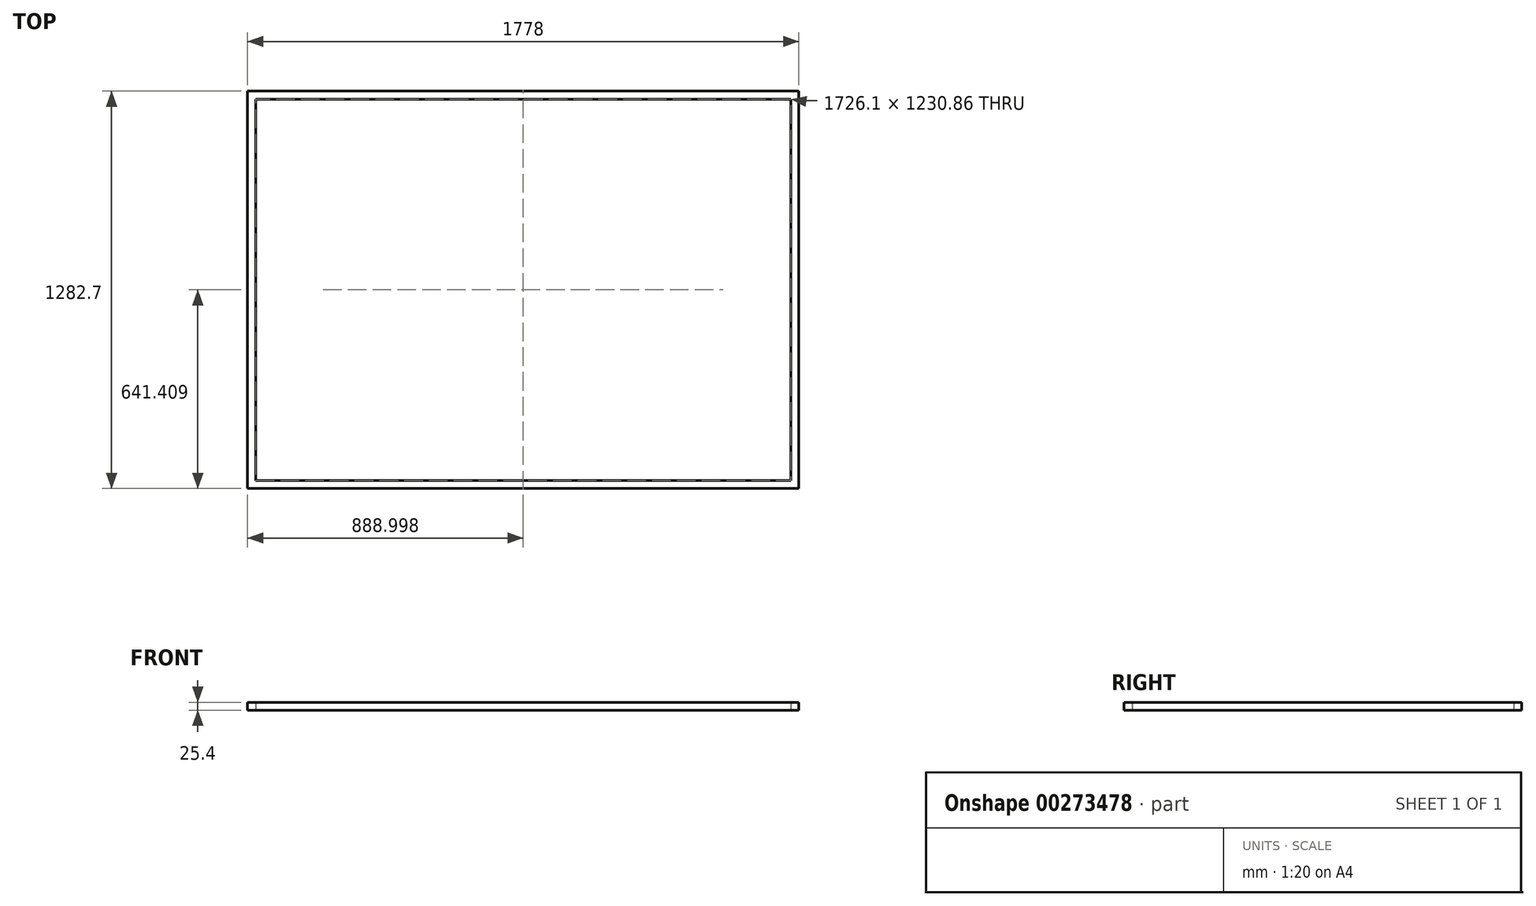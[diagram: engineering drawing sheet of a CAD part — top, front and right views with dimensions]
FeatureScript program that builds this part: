
annotation { "Feature Type Name" : "Feature", "Feature Type Description" : "" }
export const myFeature = defineFeature(function(context is Context, id is Id, definition is map)
    precondition{}
    {
        {
            var Q0;
            Q0=qCreatedBy(makeId("Top.planeOp"),FACE);
            var sketch = newSketch(context, id + "F0", { "sketchPlane" : qUnion([Q0])});
            skLineSegment(sketch, "E0.bottom", {"start": v(-847.68, 170.3) * mm, "end": v(930.32, 170.3) * mm});
            skLineSegment(sketch, "E0.top", {"start": v(-847.68, -1112.4) * mm, "end": v(930.32, -1112.4) * mm});
            skLineSegment(sketch, "E0.left", {"start": v(-847.68, 170.3) * mm, "end": v(-847.68, -1112.4) * mm});
            skLineSegment(sketch, "E0.right", {"start": v(930.32, 170.3) * mm, "end": v(930.32, -1112.4) * mm});
            skLineSegment(sketch, "E1", {"start": v(-529.22, 170.3) * mm, "end": v(-529.22, -1112.4) * mm});
            skLineSegment(sketch, "E2", {"start": v(-529.22, -1112.4) * mm, "end": v(-503.16, -1112.4) * mm});
            skLineSegment(sketch, "E3", {"start": v(-503.16, -1112.4) * mm, "end": v(-503.16, 170.3) * mm});
            skLineSegment(sketch, "E4", {"start": v(-503.16, 170.3) * mm, "end": v(-529.22, 170.3) * mm});
            skLineSegment(sketch, "E5", {"start": v(-847.68, 170.3) * mm, "end": v(-821.73, 170.3) * mm});
            skLineSegment(sketch, "E6", {"start": v(-821.73, 170.3) * mm, "end": v(-821.73, -1112.4) * mm});
            skLineSegment(sketch, "E7", {"start": v(-821.73, -1112.4) * mm, "end": v(-847.68, -1112.4) * mm});
            skLineSegment(sketch, "E8", {"start": v(930.32, 170.3) * mm, "end": v(904.37, 170.3) * mm});
            skLineSegment(sketch, "E9", {"start": v(904.37, 170.3) * mm, "end": v(904.37, -1112.4) * mm});
            skLineSegment(sketch, "E10", {"start": v(904.37, -1112.4) * mm, "end": v(930.32, -1112.4) * mm});
            skLineSegment(sketch, "E11", {"start": v(-847.68, 170.3) * mm, "end": v(-847.68, 144.44) * mm});
            skLineSegment(sketch, "E12", {"start": v(-847.68, 144.44) * mm, "end": v(930.32, 144.44) * mm});
            skLineSegment(sketch, "E13", {"start": v(930.32, 144.44) * mm, "end": v(930.32, 170.3) * mm});
            skLineSegment(sketch, "E14", {"start": v(-847.68, -1112.4) * mm, "end": v(-847.68, -1086.42) * mm});
            skLineSegment(sketch, "E15", {"start": v(-847.68, -1086.42) * mm, "end": v(930.32, -1086.42) * mm});
            skLineSegment(sketch, "E16", {"start": v(930.32, -1086.42) * mm, "end": v(930.32, -1112.4) * mm});
            skLineSegment(sketch, "E17", {"start": v(-225.13, 144.44) * mm, "end": v(-225.13, -1086.42) * mm});
            skLineSegment(sketch, "E18", {"start": v(-225.13, -1086.42) * mm, "end": v(-199.06, -1086.42) * mm});
            skLineSegment(sketch, "E19", {"start": v(-199.06, -1086.42) * mm, "end": v(-199.06, 144.44) * mm});
            skLineSegment(sketch, "E20", {"start": v(99.24, -1112.4) * mm, "end": v(99.24, 170.3) * mm});
            skLineSegment(sketch, "E21", {"start": v(99.24, 170.3) * mm, "end": v(125.3, 170.3) * mm});
            skLineSegment(sketch, "E22", {"start": v(125.3, 170.3) * mm, "end": v(125.3, -1112.4) * mm});
            skLineSegment(sketch, "E23", {"start": v(125.3, -1112.4) * mm, "end": v(99.24, -1112.4) * mm});
            skSolve(sketch);
        }
        {
            var Q0;
            Q0 = qSketchRegion(id + "F0", true);
            extrude(context, id + "F1", {"entities" : qUnion([Q0]), "depth" : 25.4 * mm});
        }
    });
